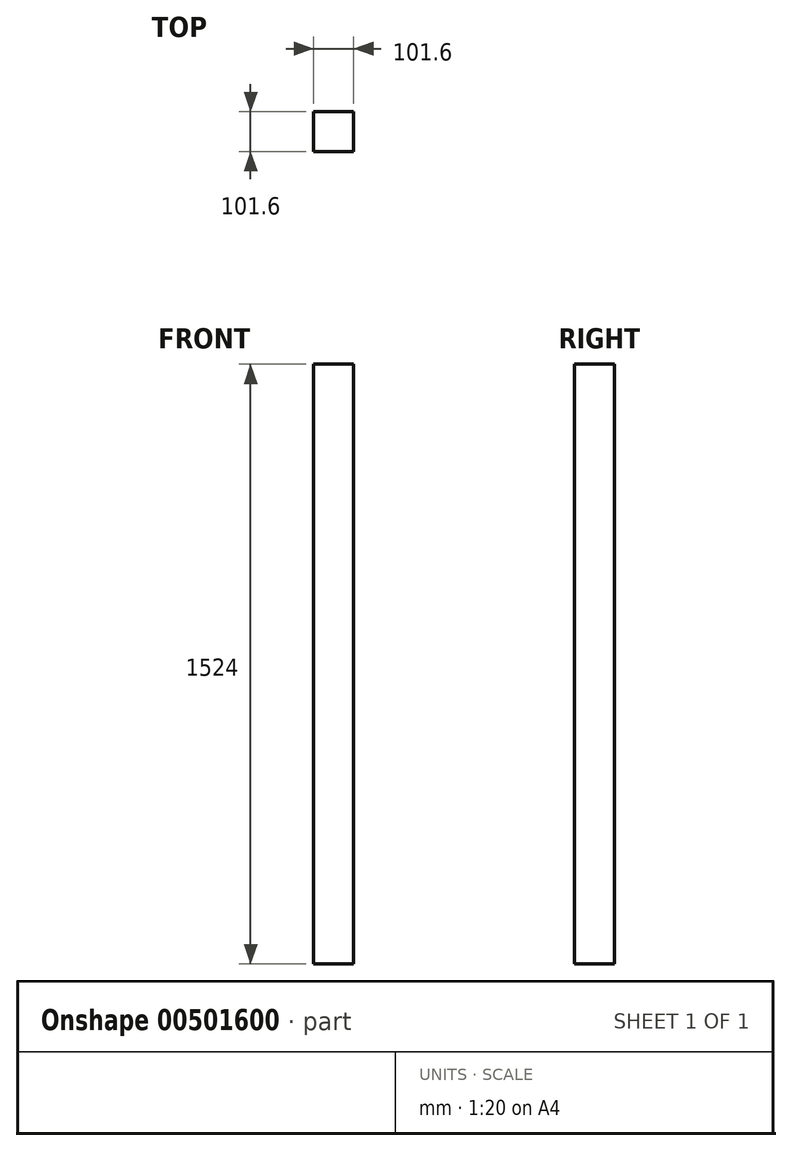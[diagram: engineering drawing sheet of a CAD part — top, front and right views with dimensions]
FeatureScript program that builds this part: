
annotation { "Feature Type Name" : "Feature", "Feature Type Description" : "" }
export const myFeature = defineFeature(function(context is Context, id is Id, definition is map)
    precondition{}
    {
        {
            var Q0;
            Q0=qCreatedBy(makeId("Front.planeOp"),FACE);
            var sketch = newSketch(context, id + "F0", { "sketchPlane" : qUnion([Q0])});
            skLineSegment(sketch, "E0.bottom", {"start": v(-54.79, -74.76) * mm, "end": v(46.81, -74.76) * mm});
            skLineSegment(sketch, "E0.top", {"start": v(-54.79, 1449.24) * mm, "end": v(46.81, 1449.24) * mm});
            skLineSegment(sketch, "E0.left", {"start": v(-54.79, -74.76) * mm, "end": v(-54.79, 1449.24) * mm});
            skLineSegment(sketch, "E0.right", {"start": v(46.81, -74.76) * mm, "end": v(46.81, 1449.24) * mm});
            skSolve(sketch);
        }
        {
            var Q0;
            Q0=makeQuery(id+"F0.imprint","IMPRINT",FACE,{"disambiguationData":[TD([[makeQuery(id+"F0.imprint","IMPRINT",EDGE,{"derivedFrom":sQuery(id+"F0.wireOp",EDGE,"E0.bottom")}),1.0]])]});
            extrude(context, id + "F1", {"entities" : qUnion([Q0]), "depth" : 101.6 * mm, "offsetDistance" : 25.4 * mm});
        }
    });
